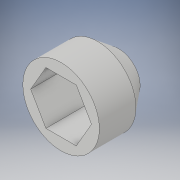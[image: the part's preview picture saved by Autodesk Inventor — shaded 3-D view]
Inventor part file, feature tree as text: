
AUTODESK INVENTOR PART (.ipt)
format: ipt  version: 2019 (Build 230136000, 136)  size: 132,608 bytes
history: native  units: mm
features: sketch x5, extrude x2, loft x1, revolve x1
ambient origin geometry x8: Origin, YZ Plane, XZ Plane, XY Plane, X Axis, Y Axis, Z Axis, Center Point
bodies: Solid1 (feature_tree)
feature tree (9):
  extrude  "Extrusion1"  Depth=6.8mm TaperAngle=0.0deg
  extrude  "Extrusion2"  Depth=6.2mm
  loft  "Loft1"
  revolve  "Revolution1"  Angle=90.0deg
  sketch  "Sketch1"  dims[d0=9.0mm d1=6.8mm d2=0.0mm]
  sketch  "Sketch2"  dims[d3=6.2mm d4=6.2mm]
  sketch  "Sketch3"  dims[d5=5.3mm d6=0.0mm d7=2.5mm]
  sketch  "Sketch4"  dims[d8=6.2mm d9=0.0mm d10=90.0deg]
  sketch  "Sketch5"  dims[d11=0.0mm d12=90.0deg d14=2.5mm d15=2.0mm d16=90.0deg]
